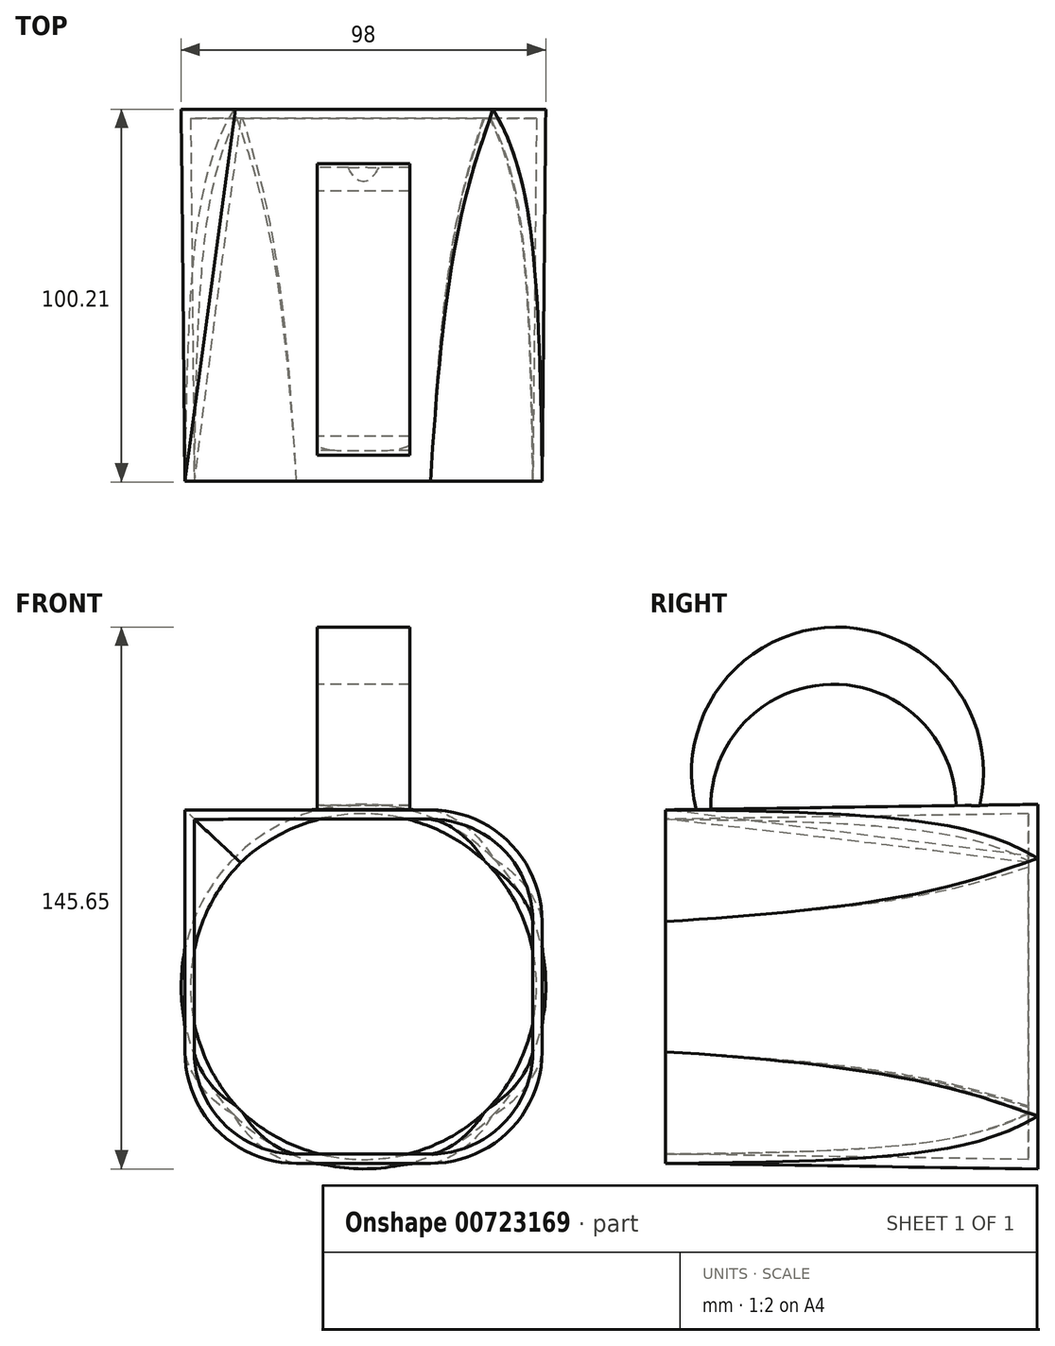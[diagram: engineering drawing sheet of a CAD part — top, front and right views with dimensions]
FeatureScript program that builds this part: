
annotation { "Feature Type Name" : "Feature", "Feature Type Description" : "" }
export const myFeature = defineFeature(function(context is Context, id is Id, definition is map)
    precondition{}
    {
        {
            var Q0;
            Q0=qCreatedBy(makeId("Front.planeOp"),FACE);
            cPlane(context, id + "F0", {"entities" : qUnion([Q0]), "cplaneType" : CPlaneType.OFFSET, "offset" : 100 * mm, "width" : 150 * mm, "height" : 150 * mm});
        }
        {
            var Q0;
            Q0=qCreatedBy(makeId("Front.planeOp"),FACE);
            var sketch = newSketch(context, id + "F1", { "sketchPlane" : qUnion([Q0])});
            skCircle(sketch, "E0", {"center": v(0, 0) * mm, "radius": 49 * mm});
            skSolve(sketch);
        }
        {
            var Q0;
            Q0=qCreatedBy(id+"F0.planeOp",FACE);
            var sketch = newSketch(context, id + "F2", { "sketchPlane" : qUnion([Q0])});
            skLineSegment(sketch, "E1.bottom", {"start": v(48, 47.5) * mm, "end": v(-48, 47.5) * mm});
            skLineSegment(sketch, "E1.top", {"start": v(48, -47.5) * mm, "end": v(-48, -47.5) * mm});
            skLineSegment(sketch, "E1.left", {"start": v(48, 47.5) * mm, "end": v(48, -47.5) * mm});
            skLineSegment(sketch, "E1.right", {"start": v(-48, 47.5) * mm, "end": v(-48, -47.5) * mm});
            skPoint(sketch, "E1.middle", {"position": v(0, 0) * mm});
            skSolve(sketch);
        }
        {
            var Q0;
            Q0=makeQuery(id+"F1.imprint","IMPRINT",FACE,{"disambiguationData":[TD([[makeQuery(id+"F1.imprint","IMPRINT",EDGE,{"derivedFrom":sQuery(id+"F1.wireOp",EDGE,"E0")}),1.0]])]});
            var Q1;
            Q1=makeQuery(id+"F2.imprint","IMPRINT",FACE,{"disambiguationData":[TD([[makeQuery(id+"F2.imprint","IMPRINT",EDGE,{"derivedFrom":sQuery(id+"F2.wireOp",EDGE,"E1.bottom")}),1.0]])]});
            loft(context, id + "F3", {"sheetProfilesArray" : [{ "sheetProfileEntities" : qUnion([Q0]) }, { "sheetProfileEntities" : qUnion([Q1]) }]});
        }
        {
            var Q0;
            Q0=makeQuery(id+"F3.opLoft","SWEPT_EDGE",EDGE,{"disambiguationData":[OSD([sQuery(id+"F1.wireOp",EDGE,"E0"),sQuery(id+"F2.wireOp",EDGE,"E1.bottom"),sQuery(id+"F2.wireOp",EDGE,"E1.left"),sQuery(id+"F2.wireOp",EDGE,"E1.right")])]});
            var Q1;
            Q1=makeQuery(id+"F3.opLoft","SWEPT_EDGE",EDGE,{"disambiguationData":[OSD([sQuery(id+"F1.wireOp",EDGE,"E0"),sQuery(id+"F2.wireOp",EDGE,"E1.bottom"),sQuery(id+"F2.wireOp",EDGE,"E1.top"),sQuery(id+"F2.wireOp",EDGE,"E1.right")])]});
            var Q2;
            Q2=makeQuery(id+"F3.opLoft","SWEPT_EDGE",EDGE,{"disambiguationData":[OSD([sQuery(id+"F2.wireOp",EDGE,"E1.bottom"),sQuery(id+"F2.wireOp",EDGE,"E1.left")])]});
            var Q3;
            Q3=makeQuery(id+"F3.opLoft","SWEPT_EDGE",EDGE,{"disambiguationData":[OSD([sQuery(id+"F1.wireOp",EDGE,"E0"),sQuery(id+"F2.wireOp",EDGE,"E1.top"),sQuery(id+"F2.wireOp",EDGE,"E1.left"),sQuery(id+"F2.wireOp",EDGE,"E1.right")])]});
            fillet(context, id + "F4", {"entities" : qUnion([Q0, Q1, Q2, Q3]), "radius" : 30 * mm, "tangentPropagation" : true, "allowEdgeOverflow" : false});
        }
        {
            var Q0;
            Q0=makeQuery(id+"F3.opLoft","CAP_FACE",FACE,{"disambiguationData":[OSD([makeQuery(id+"F2.imprint","IMPRINT",FACE,{"disambiguationData":[TD([[makeQuery(id+"F2.imprint","IMPRINT",EDGE,{"derivedFrom":sQuery(id+"F2.wireOp",EDGE,"E1.bottom")}),1.0]])]})])],"isStart":true});
            shell(context, id + "F5", {"entities" : qUnion([Q0]), "thickness" : 2.5 * mm});
        }
        {
            var Q0;
            Q0=qCreatedBy(makeId("Right.planeOp"),FACE);
            var sketch = newSketch(context, id + "F6", { "sketchPlane" : qUnion([Q0])});
            skArc(sketch, "E2", {"start": v(-21.98, 48.76) * mm, "mid": v(-55.6, 81.29) * mm, "end": v(-87.9, 47.45) * mm});
            skArc(sketch, "E3", {"start": v(-15.63, 48.63) * mm, "mid": v(-54.39, 96.65) * mm, "end": v(-91.8, 47.59) * mm});
            skLineSegment(sketch, "E4", {"start": v(-21.98, 48.76) * mm, "end": v(-15.63, 48.63) * mm});
            skLineSegment(sketch, "E5", {"start": v(-91.8, 47.59) * mm, "end": v(-87.9, 47.45) * mm});
            skSolve(sketch);
        }
        {
            var Q0;
            Q0=makeQuery(id+"F6.imprint","IMPRINT",FACE,{"disambiguationData":[TD([[makeQuery(id+"F6.imprint","IMPRINT",EDGE,{"derivedFrom":sQuery(id+"F6.wireOp",EDGE,"E2")}),-1.0]])]});
            extrude(context, id + "F7", {"entities" : qUnion([Q0]), "operationType" : NewBodyOperationType.ADD, "endBound" : BoundingType.SYMMETRIC, "depth" : 25 * mm, "offsetDistance" : 25 * mm});
        }
    });
